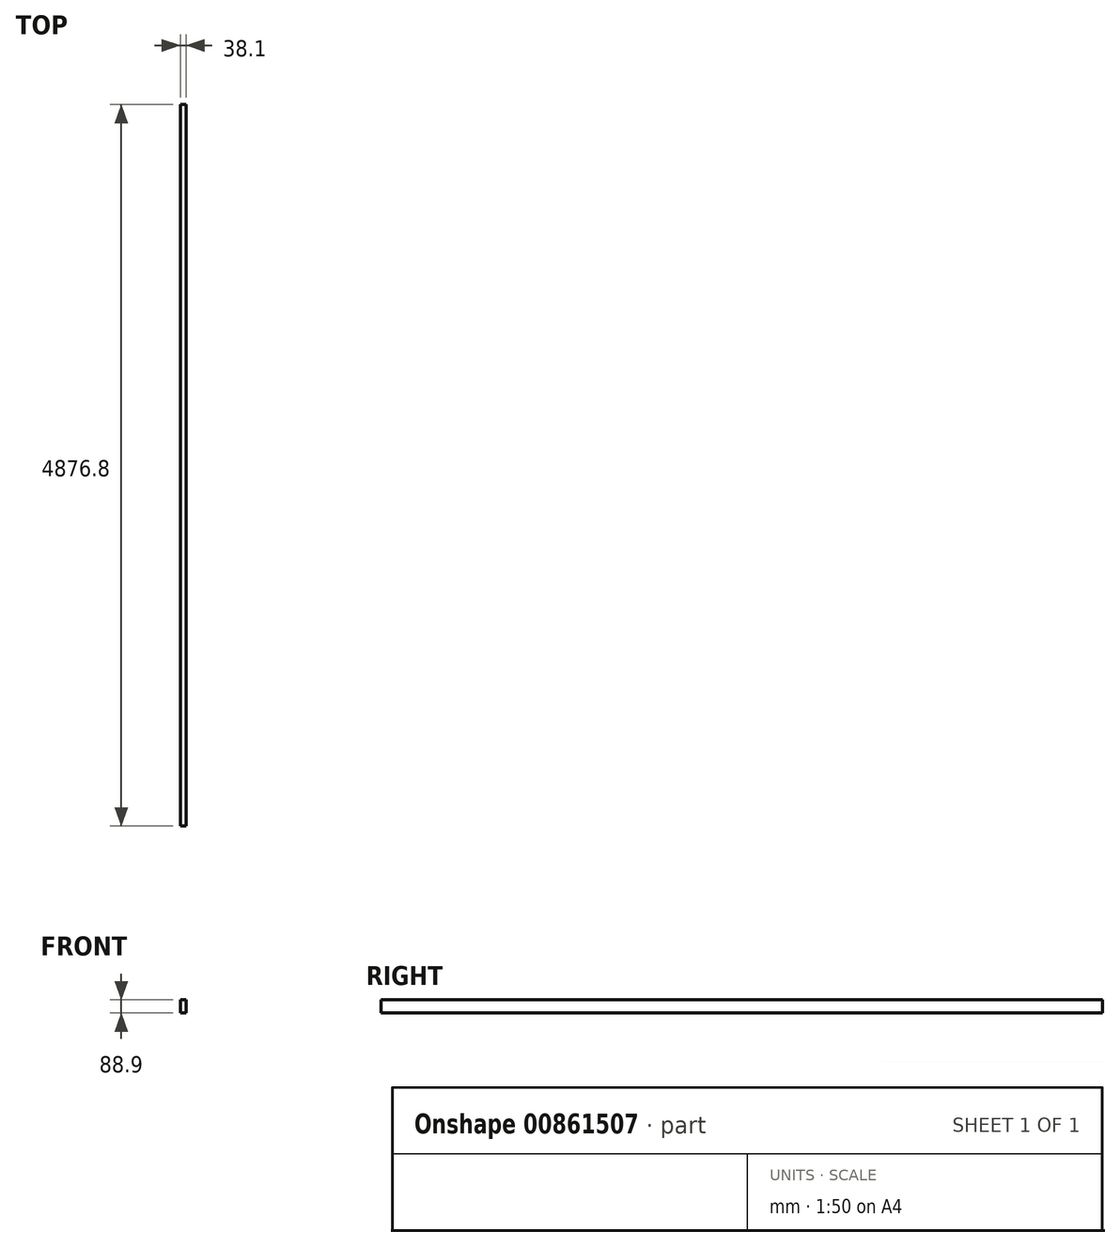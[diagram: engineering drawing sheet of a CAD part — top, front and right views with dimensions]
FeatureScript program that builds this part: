
annotation { "Feature Type Name" : "Feature", "Feature Type Description" : "" }
export const myFeature = defineFeature(function(context is Context, id is Id, definition is map)
    precondition{}
    {
        {
            var Q0;
            Q0=qCreatedBy(makeId("Front.planeOp"),FACE);
            var sketch = newSketch(context, id + "F0", { "sketchPlane" : qUnion([Q0])});
            skLineSegment(sketch, "E0.bottom", {"start": v(-19.05, 44.45) * mm, "end": v(19.05, 44.45) * mm});
            skLineSegment(sketch, "E0.top", {"start": v(-19.05, -44.45) * mm, "end": v(19.05, -44.45) * mm});
            skLineSegment(sketch, "E0.left", {"start": v(-19.05, 44.45) * mm, "end": v(-19.05, -44.45) * mm});
            skLineSegment(sketch, "E0.right", {"start": v(19.05, 44.45) * mm, "end": v(19.05, -44.45) * mm});
            skPoint(sketch, "E0.middle", {"position": v(0, 0) * mm});
            skSolve(sketch);
        }
        {
            var Q0;
            Q0=makeQuery(id+"F0.imprint","IMPRINT",FACE,{"disambiguationData":[TD([[makeQuery(id+"F0.imprint","IMPRINT",EDGE,{"derivedFrom":sQuery(id+"F0.wireOp",EDGE,"E0.bottom")}),-1.0]])]});
            extrude(context, id + "F1", {"entities" : qUnion([Q0]), "depth" : 4876.8 * mm, "offsetDistance" : 25.4 * mm});
        }
    });
